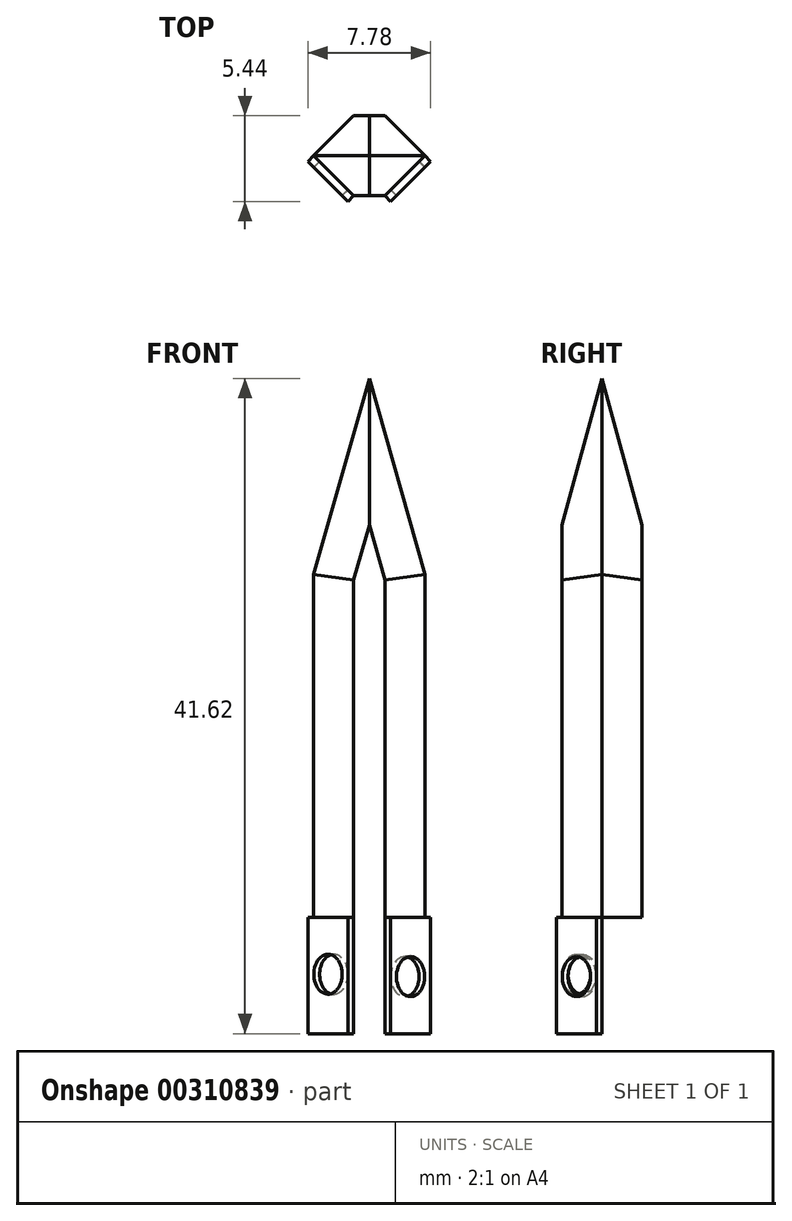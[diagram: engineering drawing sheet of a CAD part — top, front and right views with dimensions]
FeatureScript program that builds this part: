
annotation { "Feature Type Name" : "Feature", "Feature Type Description" : "" }
export const myFeature = defineFeature(function(context is Context, id is Id, definition is map)
    precondition{}
    {
        {
            var Q0;
            Q0=qCreatedBy(makeId("Front.planeOp"),FACE);
            var sketch = newSketch(context, id + "F0", { "sketchPlane" : qUnion([Q0])});
            skLineSegment(sketch, "E0", {"start": v(-6.22, 0) * mm, "end": v(-6.22, -21.76) * mm});
            skLineSegment(sketch, "E1", {"start": v(-6.22, -21.76) * mm, "end": v(-2.69, -21.76) * mm});
            skLineSegment(sketch, "E2", {"start": v(-2.69, -21.76) * mm, "end": v(-2.69, 12.45) * mm});
            skLineSegment(sketch, "E3", {"start": v(-2.69, 12.45) * mm, "end": v(-6.22, 0) * mm});
            skSolve(sketch);
        }
        {
            var Q0;
            Q0 = qSketchRegion(id + "F0", true);
            extrude(context, id + "F1", {"entities" : qUnion([Q0]), "depth" : 2.54 * mm});
        }
        {
            var Q0;
            Q0=makeQuery(id+"F1.opExtrude","CAP_EDGE",EDGE,{"disambiguationData":[OSD([sQuery(id+"F0.wireOp",EDGE,"E0")])],"isStart":false});
            var Q1;
            Q1=makeQuery(id+"F1.opExtrude","CAP_EDGE",EDGE,{"disambiguationData":[OSD([sQuery(id+"F0.wireOp",EDGE,"E3")])],"isStart":false});
            chamfer(context, id + "F2", {"entities" : qUnion([Q0, Q1]), "width" : 2.54 * mm, "tangentPropagation" : true});
        }
        {
            var Q0;
            Q0=makeQuery(id+"F1.opExtrude","SWEPT_BODY",BODY,{"disambiguationData":[OSD([sQuery(id+"F0.wireOp",EDGE,"E0"),sQuery(id+"F0.wireOp",EDGE,"E1"),sQuery(id+"F0.wireOp",EDGE,"E2"),sQuery(id+"F0.wireOp",EDGE,"E3")])]});
            var Q1;
            Q1=makeQuery(id+"F1.opExtrude","CAP_FACE",FACE,{"disambiguationData":[OSD([sQuery(id+"F0.wireOp",EDGE,"E0"),sQuery(id+"F0.wireOp",EDGE,"E1"),sQuery(id+"F0.wireOp",EDGE,"E2"),sQuery(id+"F0.wireOp",EDGE,"E3")])],"isStart":true});
            mirror(context, id + "F3", {"operationType" : NewBodyOperationType.ADD, "entities" : qUnion([Q0]), "mirrorPlane" : qUnion([Q1])});
        }
        {
            var Q0;
            Q0=makeQuery(id+"F1.opExtrude","SWEPT_BODY",BODY,{"disambiguationData":[OSD([sQuery(id+"F0.wireOp",EDGE,"E0"),sQuery(id+"F0.wireOp",EDGE,"E1"),sQuery(id+"F0.wireOp",EDGE,"E2"),sQuery(id+"F0.wireOp",EDGE,"E3")])]});
            var Q1;
            {var subQ0=makeQuery(id+"F1.opExtrude","SWEPT_FACE",FACE,{"disambiguationData":[OSD([sQuery(id+"F0.wireOp",EDGE,"E2")])]});Q1=makeQuery(id+"F3.boolean.opBoolean","MERGE",FACE,{"derivedFrom":[subQ0,makeQuery(id+"F3.opPattern","COPY",FACE,{"derivedFrom":subQ0,"instanceName":"1"})]});}
            mirror(context, id + "F4", {"operationType" : NewBodyOperationType.ADD, "entities" : qUnion([Q0]), "mirrorPlane" : qUnion([Q1])});
        }
        {
            var Q0;
            {var subQ0=makeQuery(id+"F1.opExtrude","CAP_FACE",FACE,{"disambiguationData":[OSD([sQuery(id+"F0.wireOp",EDGE,"E0"),sQuery(id+"F0.wireOp",EDGE,"E1"),sQuery(id+"F0.wireOp",EDGE,"E2"),sQuery(id+"F0.wireOp",EDGE,"E3")])],"isStart":false});Q0=makeQuery(id+"F4.boolean.opBoolean","MERGE",FACE,{"derivedFrom":[subQ0,makeQuery(id+"F4.opPattern","COPY",FACE,{"derivedFrom":subQ0,"instanceName":"1"})]});}
            var sketch = newSketch(context, id + "F5", { "sketchPlane" : qUnion([Q0])});
            skLineSegment(sketch, "E4.0", {"start": v(-2.69, 3.14) * mm, "end": v(-1.7, -0.35) * mm});
            skLineSegment(sketch, "E4.1", {"start": v(-2.69, 3.14) * mm, "end": v(-3.68, -0.35) * mm});
            skLineSegment(sketch, "E5.0", {"start": v(-1.7, -0.35) * mm, "end": v(-1.7, -21.76) * mm});
            skLineSegment(sketch, "E6.0", {"start": v(-3.68, -0.35) * mm, "end": v(-3.68, -21.76) * mm});
            skSolve(sketch);
        }
        {
            var Q0;
            Q0=makeQuery(id+"F4.opPattern","COPY",FACE,{"derivedFrom":makeQuery(id+"F2.opChamfer","BLEND_FACE",FACE,{"disambiguationData":[OSD([sQuery(id+"F0.wireOp",EDGE,"E0")])]}),"instanceName":"1"});
            var sketch = newSketch(context, id + "F6", { "sketchPlane" : qUnion([Q0])});
            skLineSegment(sketch, "E7.0.2", {"start": v(-3, -21.76) * mm, "end": v(-3, -0.35) * mm});
            skLineSegment(sketch, "E8", {"start": v(-3, -21.76) * mm, "end": v(-3, -29.17) * mm});
            skLineSegment(sketch, "E9", {"start": v(-3, -29.17) * mm, "end": v(0.6, -29.17) * mm});
            skLineSegment(sketch, "E10", {"start": v(0.6, -29.17) * mm, "end": v(0.6, -21.76) * mm});
            skCircle(sketch, "E11", {"center": v(-1.2, -25.54) * mm, "radius": 1.27 * mm});
            skPoint(sketch, "E11.centerSnap0", {"position": v(-1.2, -29.17) * mm});
            skSolve(sketch);
        }
        {
            var Q0;
            Q0=makeQuery(id+"F5.imprint","IMPRINT",FACE,{"disambiguationData":[TD([[makeQuery(id+"F5.imprint","IMPRINT",EDGE,{"derivedFrom":sQuery(id+"F5.wireOp",EDGE,"E4.0")}),-1.0]])]});
            extrude(context, id + "F7", {"entities" : qUnion([Q0]), "operationType" : NewBodyOperationType.REMOVE, "oppositeDirection" : true, "depth" : 22.86 * mm});
        }
        {
            var Q0;
            Q0=makeQuery(id+"F2.opChamfer","BLEND_FACE",FACE,{"disambiguationData":[OSD([sQuery(id+"F0.wireOp",EDGE,"E0")])]});
            var sketch = newSketch(context, id + "F8", { "sketchPlane" : qUnion([Q0])});
            skLineSegment(sketch, "E12", {"start": v(-4.4, -21.76) * mm, "end": v(-4.4, -29.17) * mm});
            skLineSegment(sketch, "E13", {"start": v(-4.4, -29.17) * mm, "end": v(-0.8, -29.17) * mm});
            skLineSegment(sketch, "E14", {"start": v(-0.8, -29.17) * mm, "end": v(-0.8, -21.76) * mm});
            skCircle(sketch, "E15", {"center": v(-2.6, -25.4) * mm, "radius": 1.27 * mm});
            skPoint(sketch, "E15.centerSnap0", {"position": v(-2.6, -29.17) * mm});
            skSolve(sketch);
        }
        {
            var Q0;
            Q0=makeQuery(id+"F8.imprint","IMPRINT",FACE,{"disambiguationData":[TD([[makeQuery(id+"F8.imprint","IMPRINT",EDGE,{"derivedFrom":sQuery(id+"F8.wireOp",EDGE,"E12")}),1.0]])]});
            extrude(context, id + "F9", {"entities" : qUnion([Q0]), "depth" : 0.5 * mm});
        }
        {
            var Q0;
            Q0=makeQuery(id+"F6.imprint","IMPRINT",FACE,{"disambiguationData":[TD([[makeQuery(id+"F6.imprint","IMPRINT",EDGE,{"derivedFrom":sQuery(id+"F6.wireOp",EDGE,"E8")}),1.0]])]});
            extrude(context, id + "F10", {"entities" : qUnion([Q0]), "depth" : 0.5 * mm});
        }
    });
